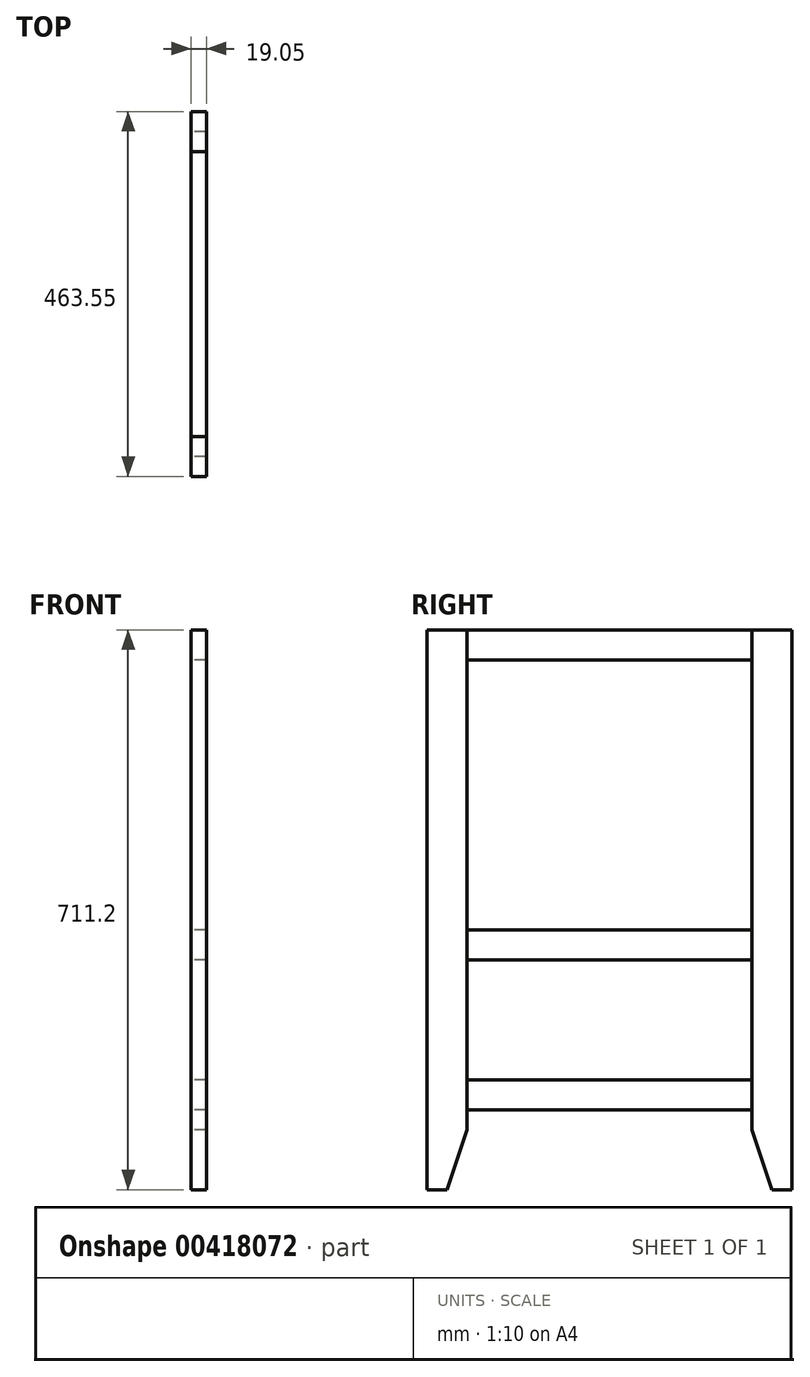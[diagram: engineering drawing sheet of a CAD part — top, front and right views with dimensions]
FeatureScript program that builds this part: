
annotation { "Feature Type Name" : "Feature", "Feature Type Description" : "" }
export const myFeature = defineFeature(function(context is Context, id is Id, definition is map)
    precondition{}
    {
        {
            var Q0;
            Q0=qCreatedBy(makeId("Right.planeOp"),FACE);
            var sketch = newSketch(context, id + "F0", { "sketchPlane" : qUnion([Q0])});
            skLineSegment(sketch, "E0.bottom", {"start": v(-431.8, 332.05) * mm, "end": v(-482.6, 332.05) * mm});
            skLineSegment(sketch, "E0.top", {"start": v(-457.2, -379.15) * mm, "end": v(-482.6, -379.15) * mm});
            skLineSegment(sketch, "E0.left", {"start": v(-431.8, 332.05) * mm, "end": v(-431.8, -302.95) * mm});
            skLineSegment(sketch, "E0.right", {"start": v(-482.6, 332.05) * mm, "end": v(-482.6, -379.15) * mm});
            skLineSegment(sketch, "E1.bottom", {"start": v(-19.05, 332.05) * mm, "end": v(-69.85, 332.05) * mm});
            skLineSegment(sketch, "E1.top", {"start": v(-19.05, -379.15) * mm, "end": v(-44.45, -379.15) * mm});
            skLineSegment(sketch, "E1.left", {"start": v(-19.05, 332.05) * mm, "end": v(-19.05, -379.15) * mm});
            skLineSegment(sketch, "E1.right", {"start": v(-69.85, 332.05) * mm, "end": v(-69.85, -302.95) * mm});
            skLineSegment(sketch, "E2.bottom", {"start": v(-431.8, 332.05) * mm, "end": v(-69.85, 332.05) * mm});
            skLineSegment(sketch, "E2.top", {"start": v(-431.8, 293.95) * mm, "end": v(-69.85, 293.95) * mm});
            skLineSegment(sketch, "E2.left", {"start": v(-431.8, 332.05) * mm, "end": v(-431.8, 293.95) * mm});
            skLineSegment(sketch, "E2.right", {"start": v(-69.85, 332.05) * mm, "end": v(-69.85, 293.95) * mm});
            skLineSegment(sketch, "E3.bottom", {"start": v(-69.85, -48.95) * mm, "end": v(-431.8, -48.95) * mm});
            skLineSegment(sketch, "E3.top", {"start": v(-69.85, -87.05) * mm, "end": v(-431.8, -87.05) * mm});
            skLineSegment(sketch, "E3.left", {"start": v(-69.85, -48.95) * mm, "end": v(-69.85, -87.05) * mm});
            skLineSegment(sketch, "E3.right", {"start": v(-431.8, -48.95) * mm, "end": v(-431.8, -87.05) * mm});
            skLineSegment(sketch, "E4.bottom", {"start": v(-69.85, -239.45) * mm, "end": v(-431.8, -239.45) * mm});
            skLineSegment(sketch, "E4.top", {"start": v(-69.85, -277.55) * mm, "end": v(-431.8, -277.55) * mm});
            skLineSegment(sketch, "E4.left", {"start": v(-69.85, -239.45) * mm, "end": v(-69.85, -277.55) * mm});
            skLineSegment(sketch, "E4.right", {"start": v(-431.8, -239.45) * mm, "end": v(-431.8, -277.55) * mm});
            skLineSegment(sketch, "E5.bottom", {"start": v(-269.88, 293.95) * mm, "end": v(-231.78, 293.95) * mm});
            skLineSegment(sketch, "E5.top", {"start": v(-269.87, -48.95) * mm, "end": v(-231.77, -48.95) * mm});
            skLineSegment(sketch, "E5.left", {"start": v(-269.88, 293.95) * mm, "end": v(-269.87, -48.95) * mm});
            skLineSegment(sketch, "E5.right", {"start": v(-231.78, 293.95) * mm, "end": v(-231.77, -48.95) * mm});
            skLineSegment(sketch, "E6", {"start": v(-457.2, -379.15) * mm, "end": v(-431.8, -302.95) * mm});
            skPoint(sketch, "E7.orphan", {"position": v(-431.8, -379.15) * mm});
            skLineSegment(sketch, "E8", {"start": v(-44.45, -379.15) * mm, "end": v(-69.85, -302.95) * mm});
            skPoint(sketch, "E9.orphan", {"position": v(-69.85, -379.15) * mm});
            skSolve(sketch);
        }
        {
            var Q0;
            Q0=makeQuery(id+"F0.imprint","IMPRINT",FACE,{"disambiguationData":[TD([[makeQuery(id+"F0.imprint","IMPRINT",EDGE,{"derivedFrom":sQuery(id+"F0.wireOp",EDGE,"E0.bottom")}),1.0]])]});
            var Q1;
            Q1=makeQuery(id+"F0.imprint","IMPRINT",FACE,{"disambiguationData":[TD([[makeQuery(id+"F0.imprint","IMPRINT",EDGE,{"derivedFrom":sQuery(id+"F0.wireOp",EDGE,"E5.bottom")}),-1.0]])]});
            var Q2;
            Q2=makeQuery(id+"F0.imprint","IMPRINT",FACE,{"disambiguationData":[TD([[makeQuery(id+"F0.imprint","IMPRINT",EDGE,{"derivedFrom":sQuery(id+"F0.wireOp",EDGE,"E1.bottom")}),1.0]])]});
            extrude(context, id + "F1", {"entities" : qUnion([Q0, Q1, Q2]), "depth" : 19.05 * mm});
        }
        {
            var Q0;
            Q0=makeQuery(id+"F0.imprint","IMPRINT",FACE,{"disambiguationData":[TD([[makeQuery(id+"F0.imprint","IMPRINT",EDGE,{"derivedFrom":sQuery(id+"F0.wireOp",EDGE,"E2.bottom")}),-1.0]])]});
            var Q1;
            Q1=makeQuery(id+"F0.imprint","IMPRINT",FACE,{"disambiguationData":[TD([[makeQuery(id+"F0.imprint","IMPRINT",EDGE,{"derivedFrom":sQuery(id+"F0.wireOp",EDGE,"E3.top")}),-1.0]])]});
            var Q2;
            Q2=makeQuery(id+"F0.imprint","IMPRINT",FACE,{"disambiguationData":[TD([[makeQuery(id+"F0.imprint","IMPRINT",EDGE,{"derivedFrom":sQuery(id+"F0.wireOp",EDGE,"E4.bottom")}),1.0]])]});
            extrude(context, id + "F2", {"entities" : qUnion([Q0, Q1, Q2]), "depth" : 19.05 * mm});
        }
    });
